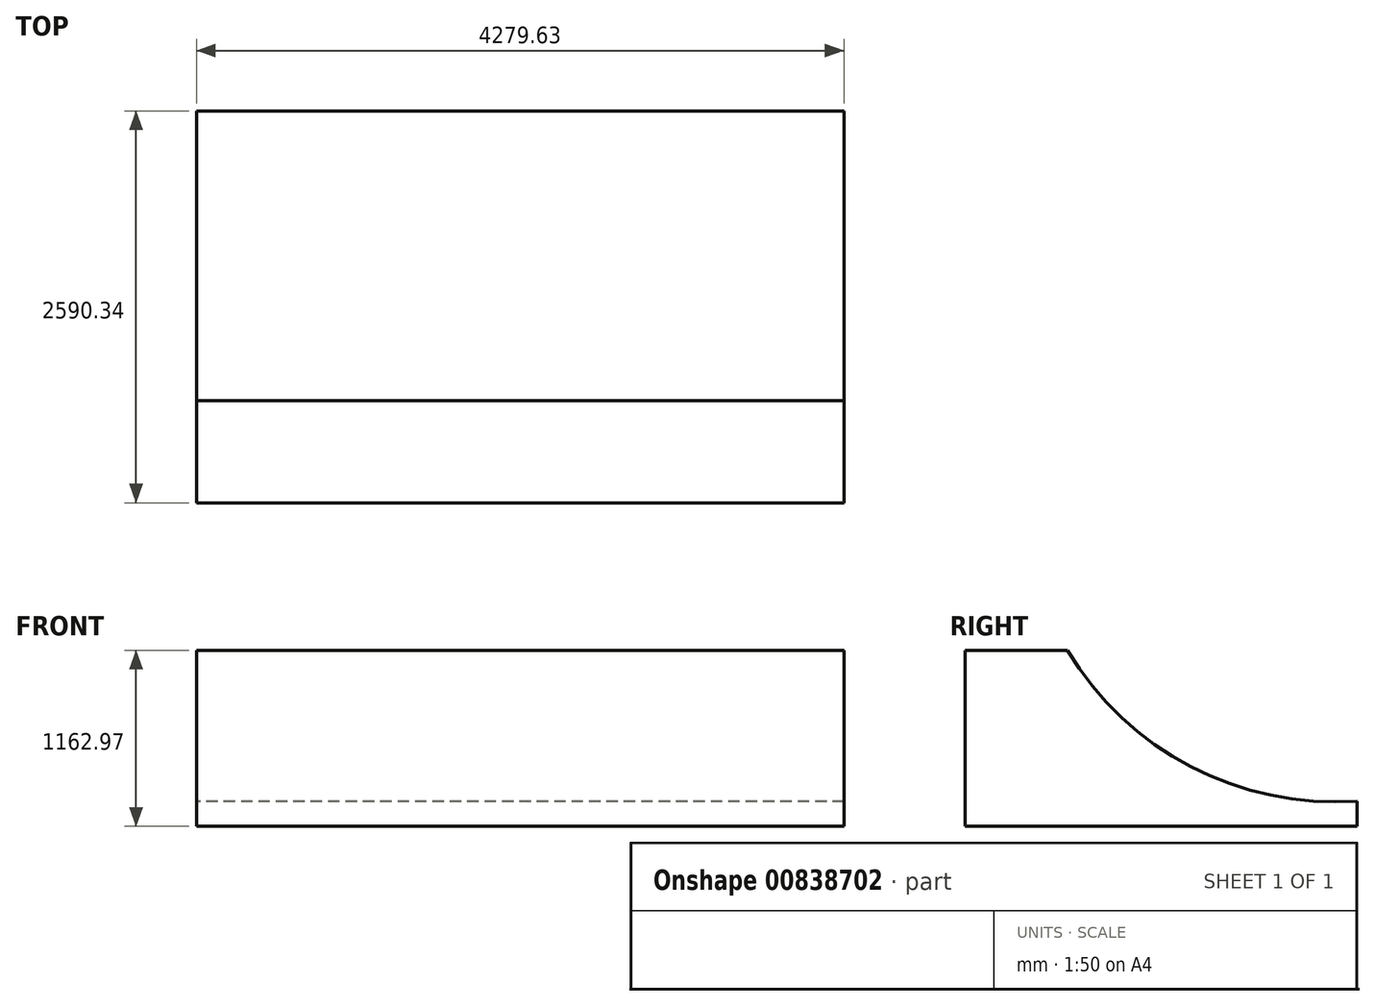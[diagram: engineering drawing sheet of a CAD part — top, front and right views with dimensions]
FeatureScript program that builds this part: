
annotation { "Feature Type Name" : "Feature", "Feature Type Description" : "" }
export const myFeature = defineFeature(function(context is Context, id is Id, definition is map)
    precondition{}
    {
        {
            var Q0;
            Q0=qCreatedBy(makeId("Right.planeOp"),FACE);
            var sketch = newSketch(context, id + "F0", { "sketchPlane" : qUnion([Q0])});
            skLineSegment(sketch, "E0", {"start": v(0, 1162.97) * mm, "end": v(0, 0) * mm});
            skLineSegment(sketch, "E1", {"start": v(0, 0) * mm, "end": v(2590.34, 0) * mm});
            skLineSegment(sketch, "E2", {"start": v(676.81, 1162.97) * mm, "end": v(0, 1162.97) * mm});
            skLineSegment(sketch, "E3", {"start": v(2590.34, 0) * mm, "end": v(2590.34, 166.52) * mm});
            skCircle(sketch, "E4", {"center": v(2444.24, 2221.5) * mm, "radius": 2060.17 * mm});
            skPoint(sketch, "E4.third.point", {"position": v(3332.43, 4080.38) * mm});
            skSolve(sketch);
        }
        {
            var Q0;
            Q0=makeQuery(id+"F0.imprint","IMPRINT",FACE,{"disambiguationData":[TD([[makeQuery(id+"F0.imprint","IMPRINT",EDGE,{"derivedFrom":sQuery(id+"F0.wireOp",EDGE,"E0")}),1.0]])]});
            extrude(context, id + "F1", {"entities" : qUnion([Q0]), "depth" : 25.4 * mm, "offsetDistance" : 25.4 * mm});
        }
        {
            var Q0;
            Q0=makeQuery(id+"F1.opExtrude","CAP_FACE",FACE,{"disambiguationData":[OSD([sQuery(id+"F0.wireOp",EDGE,"E0"),sQuery(id+"F0.wireOp",EDGE,"E1"),sQuery(id+"F0.wireOp",EDGE,"E2"),sQuery(id+"F0.wireOp",EDGE,"E3"),sQuery(id+"F0.wireOp",EDGE,"E4")])],"isStart":false});
            extrude(context, id + "F2", {"entities" : qUnion([Q0]), "operationType" : NewBodyOperationType.ADD, "depth" : 4254.23 * mm, "offsetDistance" : 25.4 * mm});
        }
    });
